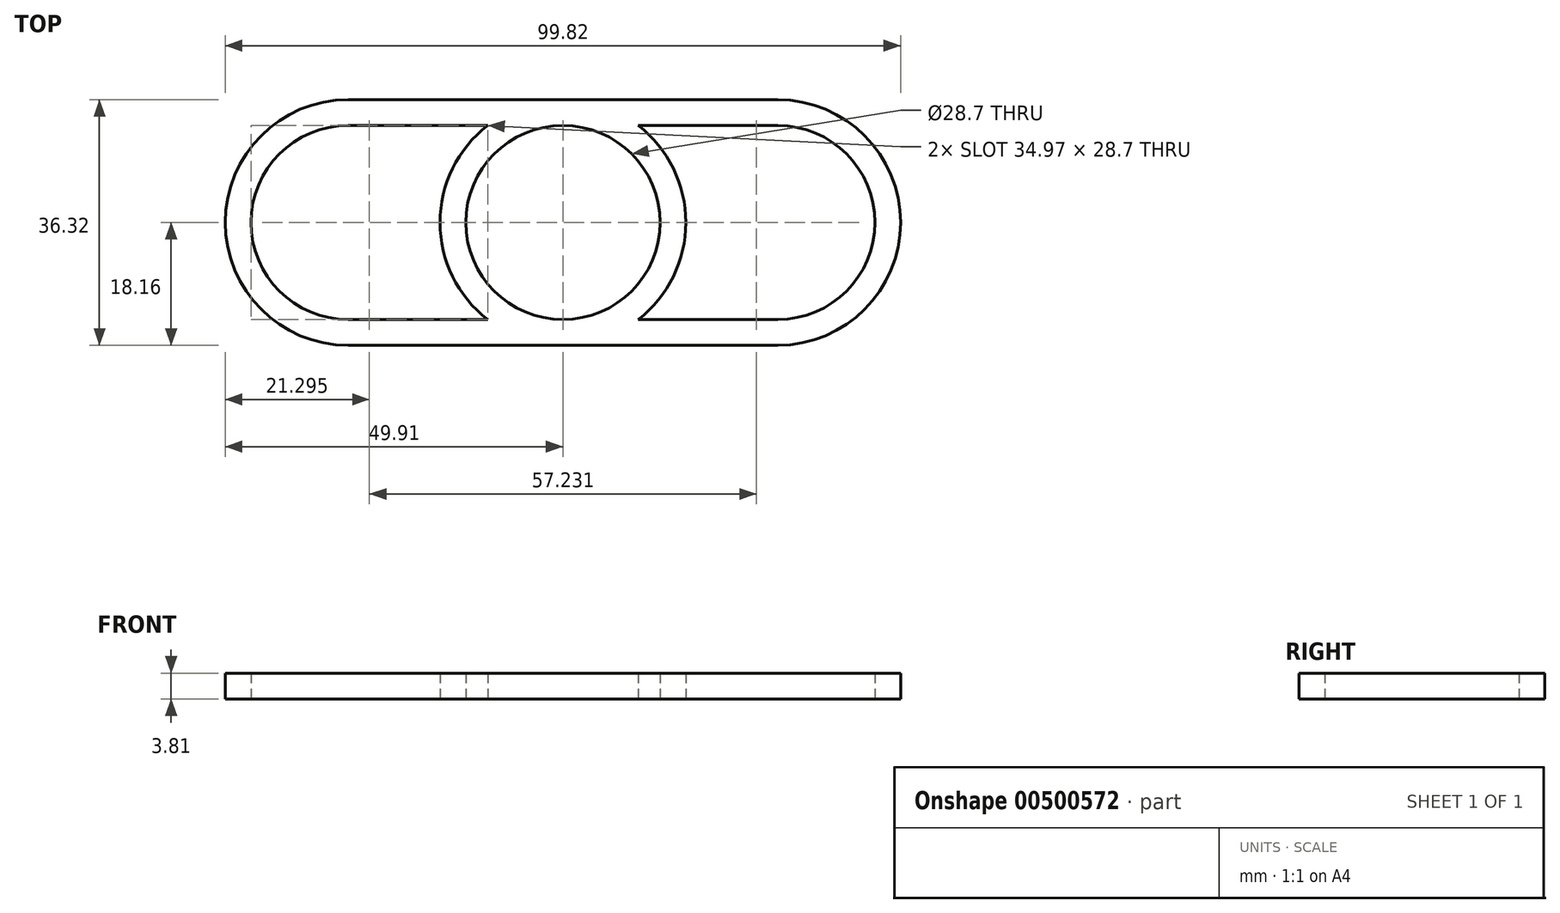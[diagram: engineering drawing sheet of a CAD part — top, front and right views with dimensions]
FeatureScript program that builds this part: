
annotation { "Feature Type Name" : "Feature", "Feature Type Description" : "" }
export const myFeature = defineFeature(function(context is Context, id is Id, definition is map)
    precondition{}
    {
        {
            var Q0;
            Q0=qCreatedBy(makeId("Top.planeOp"),FACE);
            var sketch = newSketch(context, id + "F0", { "sketchPlane" : qUnion([Q0])});
            skLineSegment(sketch, "E0.bottom", {"start": v(31.75, 18.16) * mm, "end": v(-31.75, 18.16) * mm});
            skLineSegment(sketch, "E0.top", {"start": v(31.75, -18.16) * mm, "end": v(-31.75, -18.16) * mm});
            skLineSegment(sketch, "E0.left", {"start": v(31.75, 18.16) * mm, "end": v(31.75, 14.35) * mm});
            skLineSegment(sketch, "E0.right", {"start": v(-31.75, 18.16) * mm, "end": v(-31.75, 14.35) * mm});
            skPoint(sketch, "E0.middle", {"position": v(0, 0) * mm});
            skArc(sketch, "E1", {"start": v(-31.75, 18.16) * mm, "mid": v(-49.91, 0) * mm, "end": v(-31.75, -18.16) * mm});
            skArc(sketch, "E2", {"start": v(31.75, -18.16) * mm, "mid": v(49.91, 0) * mm, "end": v(31.75, 18.16) * mm});
            skCircle(sketch, "E3", {"center": v(0, 0) * mm, "radius": 14.35 * mm});
            skArc(sketch, "E4.0", {"start": v(-31.75, 14.35) * mm, "mid": v(-46.1, 0) * mm, "end": v(-31.75, -14.35) * mm});
            skArc(sketch, "E5.0", {"start": v(31.75, -14.35) * mm, "mid": v(46.1, 0) * mm, "end": v(31.75, 14.35) * mm});
            skLineSegment(sketch, "E6.0", {"start": v(31.75, 14.35) * mm, "end": v(11.13, 14.35) * mm});
            skLineSegment(sketch, "E7.0", {"start": v(31.75, -14.35) * mm, "end": v(11.13, -14.35) * mm});
            skArc(sketch, "E8.0", {"start": v(-11.13, 14.35) * mm, "mid": v(-18.16, 0) * mm, "end": v(-11.13, -14.35) * mm});
            skLineSegment(sketch, "E9.trimOffspring", {"start": v(-11.13, 14.35) * mm, "end": v(-31.75, 14.35) * mm});
            skLineSegment(sketch, "E10.trimOffspring", {"start": v(-31.75, -14.35) * mm, "end": v(-31.75, -18.16) * mm});
            skArc(sketch, "E11.trimOffspring", {"start": v(11.13, -14.35) * mm, "mid": v(18.16, 0) * mm, "end": v(11.13, 14.35) * mm});
            skLineSegment(sketch, "E12.trimOffspring", {"start": v(-11.13, -14.35) * mm, "end": v(-31.75, -14.35) * mm});
            skLineSegment(sketch, "E13.trimOffspring", {"start": v(31.75, -14.35) * mm, "end": v(31.75, -18.16) * mm});
            skSolve(sketch);
        }
        {
            var Q0;
            Q0 = qSketchRegion(id + "F0", true);
            extrude(context, id + "F1", {"entities" : qUnion([Q0]), "depth" : 3.8 * mm});
        }
    });
